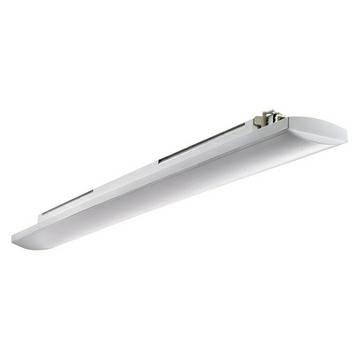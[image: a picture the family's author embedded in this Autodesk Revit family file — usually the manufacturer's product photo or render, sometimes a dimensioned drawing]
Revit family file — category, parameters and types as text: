
# Revit family: Lighting-Industrial-GEWISS-SMART[3]PLUS-WATERTIGHT-LED-EMERGENCY_OPAL_1200mm
name_source: partatom
category: Apparecchi per illuminazione
units: mm (PartAtom-declared; Revit-internal decimal feet)

## family parameters
Condiviso = No
Host = Superficie
Numero OmniClass = 23.80.70.11
Punto di calcolo locali = No
Quota connettore circolare = Usa diametro
Sorgente d'illuminazione = No
Taglio con vuoti quando caricato = No
Tipo di parte = Normale
Titolo OmniClass = Luminaries for Internal Lighting

## types (1)
- Lighting-Industrial-GEWISS-SMART[3]PLUS-WATERTIGHT-LED-EMERGENCY_OPAL_1200mm
    Application = Indoor
    Carico apparente = 45 VA
    Catalogue = LIGHTING
    Catalogue Range = SMART[3] PLUS
    Colour temperature = 5700 K (CRI > 90)
    Colour temperature: = 5700 K (CRI > 90)
    Commenti sul wattaggio = 45W
    Descrizione = SMART3 PLUS 1200 EMERG DT1+DT6 HE OPAL 9 57
    Efficiency class of integrated LEDs = A ÷ A++
    Electrocod = 2434
    Ganci = GEWISS  - ALLUMINIO
    Glow Wire Test = 850°C
    IDF = fd25af52-2ba2-488d-94b5-5296e47166b2
    IDT = c24490b2-922b-4a62-9750-73ed8a6aae65
    IP degree = IP66/IP69
    Immagine tipo = GWS3136P.jpg
    Insulation class = II
    Lamp = LED
    Lampada = LED
    Length = 1200 mm
    Lumen output (lm) = 3900
    Lunghezza Lampada = 1200 mm
    Modello = GWS3225AP957
    Operating temperature: = ND
    Produttore = GEWISS S.p.A.
    Prospetto di default = 1219 mm
    SEO = Ceiling
    Schermo. = Gewiss - Led Acceso
    Shield type = Opal
    Shock resistance = IK08
    Stampa 1_100 = Sì
    Stampa 1_200 = No
    Struttura = GEWISS - SMART 3 - GRIGIO
    System power = 36 W
    Technical sheet = https://www.gewiss.com
    Type of light source = LED - Not replaceable
    URL = https://www.gewiss.com
    Version file RFA = 20.0
    Voltage = 220-240 V
    Warranty = ND
    Working temperature = ND
